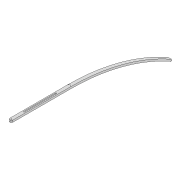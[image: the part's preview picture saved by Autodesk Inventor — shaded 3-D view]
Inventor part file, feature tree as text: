
AUTODESK INVENTOR PART (.ipt)
format: ipt  version: 2022 (Build 260153000, 153)  size: 124,416 bytes
history: native  units: mm
features: extrude x2, sketch x2, projected_geometry x2, fillet x1
ambient origin geometry x8: Origin, YZ Plane, XZ Plane, XY Plane, X Axis, Y Axis, Z Axis, Center Point
bodies: Solid1 (feature_tree)
feature tree (7):
  extrude  "Extrusion1"  Depth=10.0mm
  extrude  "Extrusion2"  Depth=2.0mm
  fillet  "Fillet1"  Radius=140.0mm
  sketch  "Sketch1"  dims[d0=180.0mm d1=10.0mm]
  sketch  "Sketch2"  dims[d2=3.3mm d3=40.0mm d5=140.0mm d6=3.3mm d7=6.0mm d8=0.0mm d9=6.0mm d10=498.004mm d11=90.0mm d12=10.0mm d13=0.0mm d14=2.0mm]
  projected_geometry  "Projected Loop1"
  projected_geometry  "Projected Loop2"
